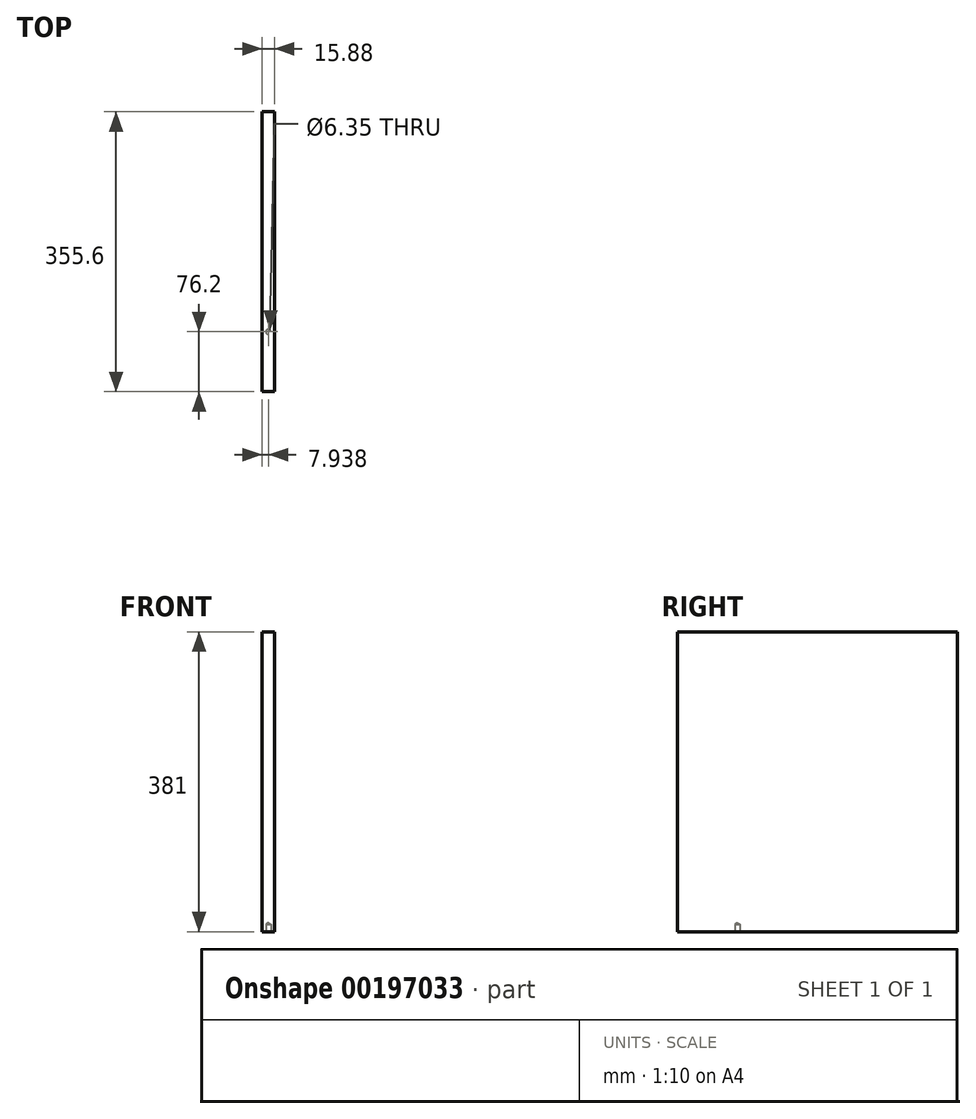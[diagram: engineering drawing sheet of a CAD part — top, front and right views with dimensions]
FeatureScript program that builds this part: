
annotation { "Feature Type Name" : "Feature", "Feature Type Description" : "" }
export const myFeature = defineFeature(function(context is Context, id is Id, definition is map)
    precondition{}
    {
        {
            var Q0;
            Q0=qCreatedBy(makeId("Right.planeOp"),FACE);
            var sketch = newSketch(context, id + "F0", { "sketchPlane" : qUnion([Q0])});
            skLineSegment(sketch, "E0.bottom", {"start": v(0, 0) * mm, "end": v(355.6, 0) * mm});
            skLineSegment(sketch, "E0.top", {"start": v(0, 381) * mm, "end": v(355.6, 381) * mm});
            skLineSegment(sketch, "E0.left", {"start": v(0, 0) * mm, "end": v(0, 381) * mm});
            skLineSegment(sketch, "E0.right", {"start": v(355.6, 0) * mm, "end": v(355.6, 381) * mm});
            skSolve(sketch);
        }
        {
            var Q0;
            Q0=makeQuery(id+"F0.imprint","IMPRINT",FACE,{"disambiguationData":[TD([[makeQuery(id+"F0.imprint","IMPRINT",EDGE,{"derivedFrom":sQuery(id+"F0.wireOp",EDGE,"E0.bottom")}),1.0]])]});
            extrude(context, id + "F1", {"entities" : qUnion([Q0]), "depth" : 15.88 * mm});
        }
        {
            var Q0;
            Q0=makeQuery(id+"F1.opExtrude","SWEPT_FACE",FACE,{"disambiguationData":[OSD([sQuery(id+"F0.wireOp",EDGE,"E0.bottom")])]});
            var sketch = newSketch(context, id + "F2", { "sketchPlane" : qUnion([Q0])});
            skLineSegment(sketch, "E1", {"start": v(7.94, 0) * mm, "end": v(7.94, -355.6) * mm, "construction": true});
            skPoint(sketch, "E2", {"position": v(7.94, -279.4) * mm});
            skPoint(sketch, "E3", {"position": v(7.94, -76.2) * mm});
            skSolve(sketch);
        }
        {
            var Q0;
            Q0=sQuery(id+"F2.wireOp",VERTEX,"E3");
            var Q1;
            Q1=makeQuery(id+"F1.opExtrude","SWEPT_BODY",BODY,{"disambiguationData":[OSD([sQuery(id+"F0.wireOp",EDGE,"E0.bottom"),sQuery(id+"F0.wireOp",EDGE,"E0.top"),sQuery(id+"F0.wireOp",EDGE,"E0.left"),sQuery(id+"F0.wireOp",EDGE,"E0.right")])]});
            hole(context, id + "F3", {"style" : HoleStyle.SIMPLE, "endStyle" : HoleEndStyle.BLIND, "holeDiameter" : 6.35 * mm, "holeDepth" : 9.52 * mm, "locations" : qUnion([Q0]), "scope" : qUnion([Q1])});
        }
    });
